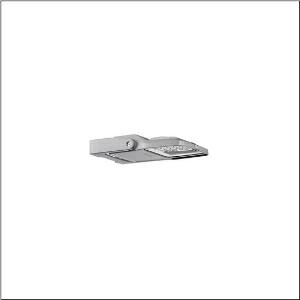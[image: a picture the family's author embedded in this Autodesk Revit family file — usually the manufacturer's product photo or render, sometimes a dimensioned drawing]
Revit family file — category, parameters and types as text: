
# Revit family: floodlight_fl_21_iq_micro___pl43_5xa7761a4a2a_9599
name_source: partatom
category: Lighting Fixtures
units: mm (PartAtom-declared; Revit-internal decimal feet)

## family parameters
Cut with Voids When Loaded = No
Host = Face
Light Source = No
Part Type = Normal
Room Calculation Point = No
Round Connector Dimension = Use Diameter
Shared = No

## types (1)
- --- (1 x LED, 3170 lm, 23.1 W, 4000K)
    Apparent Load = 23 VA
    CIE Flux Codes = 29 80 99 100 100
    Color Rendering = 70
    Color Temperature = 4000K
    Default Elevation = 1800 mm
    Description = Floodlight FL 21 iQ micro, floodlight, primary light control with lens, of PMMA, primary optical cover: protective disc, of toughened safety glass, transparent, light distribution: PL43, light emission: direct distribution, installation type: surface-mounted, LED, High Power LED, rated luminous flux: 3.170lm, luminous efficacy: 137lm/W, light colour: 740, colour temperature: 4000K, control: optimised constant luminous flux control (CLO 2.0), Desk-Remote (wireless, voltage-free reading and setting of iQ features in the workshop via application-optimized NFC function/RFID function), Light-Fading, Smart-Wire, Night-Set, Lumen-Switch, Temp-Guard, Auto-Match, with terminal, 6-pole, mains connection: 220..240V, AC, 50/60Hz, start of lifetime: 23W, end of service life: 24W, reduction: 11W, luminaire housing, of diecast aluminium, powder-coated, Siteco® metallic grey (DB 702S), corrosivity category C5 mid according to DIN EN ISO 12944, sealing non-destructively replaceable, design bracket, of diecast aluminium, powder-coated, Siteco® metallic grey (DB 702S), protection rating (complete): IP66, insulation class (complete): insulation class II (safety insulation), certification: CE, ENEC, VDE, protection symbol: D, impact resistance: IK07, permissible operating ambient temperature: -40..+40°C, permissible operating ambient temperature for outdoor applications: -40..+50°C, standard: DIN EN 12944, LABS conformity tested according to VDMA 24364:2018-05, packaging unit: 1 piece

Light Distribution: PL43
    Height = 65 mm
    Lamp = 1 x LED
    Lamp Light Flux = 3170 lm
    Lamp Power = 23.1 W
    Lamp count = 1
    Length = 312 mm
    Luminous efficacy = 137 lm/W
    Manufacturer = Siteco
    ModVariant = No
    Model = 5XA7761A4A2A
    Mounting Place = Wall
    Mounting Type = Surface mounted
    Number of Poles = 1
    OnlyDefault = Yes
    Power Factor = 1
    Product Name = Floodlight FL 21 iQ micro | PL43
    Product group = floodlight | wall mounted
    ProductGroupID = 2001
    Protection Class = Protection class II
    Protection Degree = IP 66
    RLX_Detail_Level = 1
    RLX_Emergency_Light_Flux = 0 lm
    RLX_Emergency_Type = 0
    RLX_Emergency_Type_DB = No
    RlxData = <blob elided: 97325 chars, md5=e16cedd7>
    Socket = socket
    Standby Power = 0 W
    System Light Flux = 3170 lm
    System Power = 23 W
    Type Comments = factory setting: luminous flux: 100 % | dim-lin: 254 | 455 mA
    Type Image = l_1006878.jpg
    URL = http://relux.com
    VarID = @adj_110129
    Voltage = 0 V
    Weight = 0.00 kg
    Width = 230 mm

## geometry (parser evidence)
native form markers: Blend x4, Sweep x13
no freeform markers — native parametric forms only
